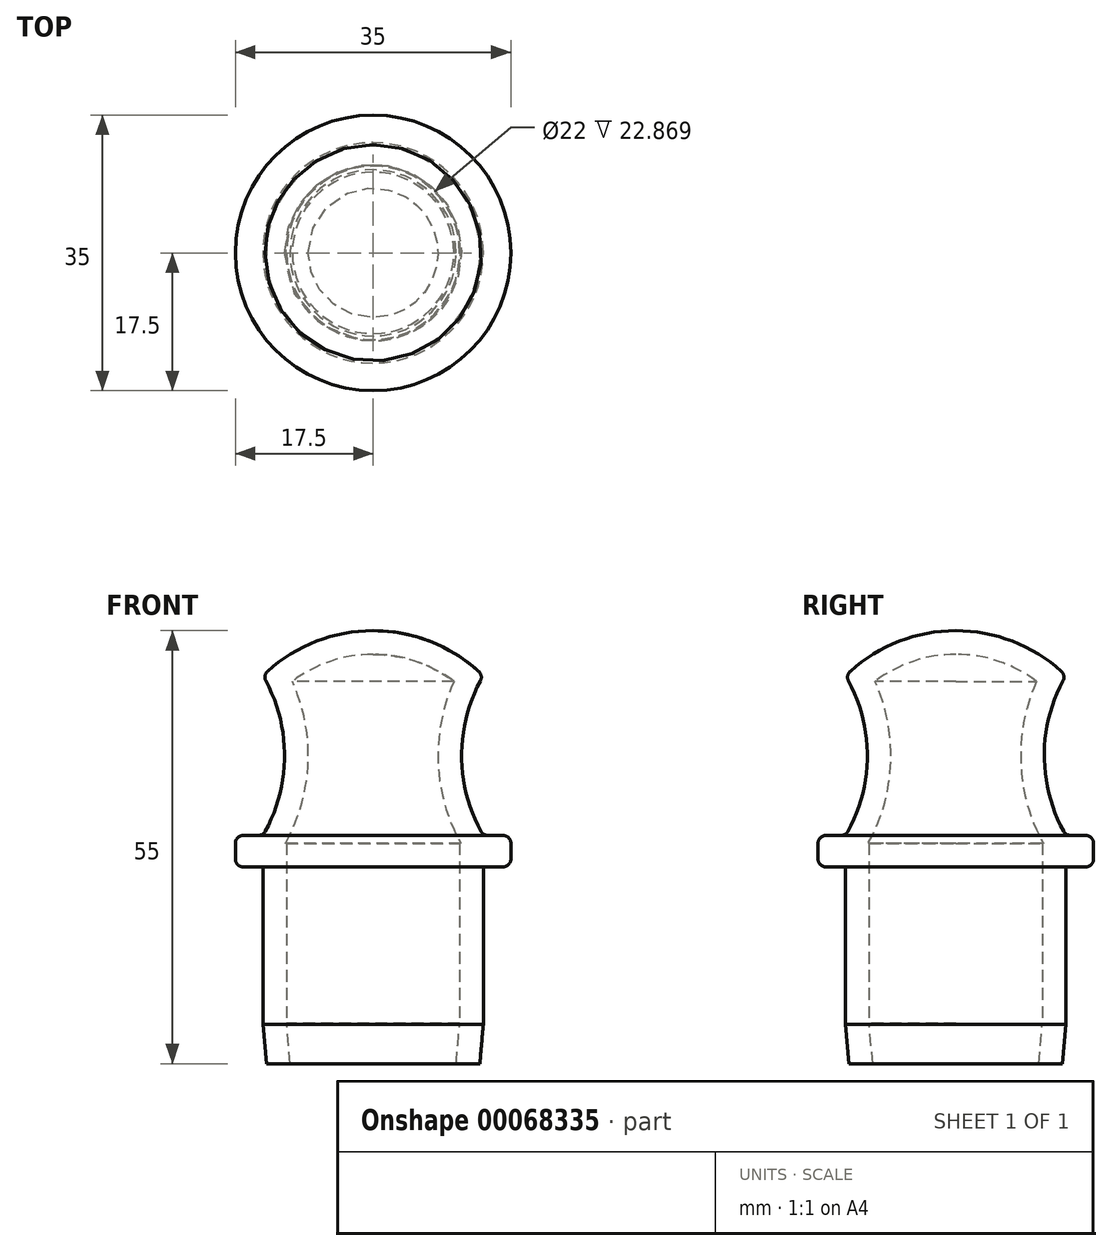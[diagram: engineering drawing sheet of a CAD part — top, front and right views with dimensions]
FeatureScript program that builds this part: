
annotation { "Feature Type Name" : "Feature", "Feature Type Description" : "" }
export const myFeature = defineFeature(function(context is Context, id is Id, definition is map)
    precondition{}
    {
        {
            var Q0;
            Q0=qCreatedBy(makeId("Top.planeOp"),FACE);
            var sketch = newSketch(context, id + "F0", { "sketchPlane" : qUnion([Q0])});
            skCircle(sketch, "E0", {"center": v(0, 0) * mm, "radius": 14 * mm});
            skSolve(sketch);
        }
        {
            var Q0;
            Q0 = qSketchRegion(id + "F0", true);
            extrude(context, id + "F1", {"entities" : qUnion([Q0]), "depth" : 25 * mm});
        }
        {
            var Q0;
            Q0=qCreatedBy(makeId("Front.planeOp"),FACE);
            var sketch = newSketch(context, id + "F2", { "sketchPlane" : qUnion([Q0])});
            skLineSegment(sketch, "E1.0.0", {"start": v(0, 25) * mm, "end": v(14, 25) * mm});
            skLineSegment(sketch, "E2", {"start": v(14, 25) * mm, "end": v(17.5, 25) * mm});
            skLineSegment(sketch, "E3", {"start": v(17.5, 25) * mm, "end": v(17.5, 29) * mm});
            skLineSegment(sketch, "E4", {"start": v(17.5, 29) * mm, "end": v(14, 29) * mm});
            skLineSegment(sketch, "E5", {"start": v(0, -0.93) * mm, "end": v(0, 40) * mm, "construction": true});
            skLineSegment(sketch, "E6", {"start": v(0, 55) * mm, "end": v(0, 25) * mm});
            skPoint(sketch, "E7.orphan", {"position": v(-14, 25) * mm});
            skArc(sketch, "E8", {"start": v(14, 49.28) * mm, "mid": v(11.24, 39.14) * mm, "end": v(14, 29) * mm});
            skArc(sketch, "E9", {"start": v(14, 49.28) * mm, "mid": v(7.56, 53.52) * mm, "end": v(0, 55) * mm});
            skSolve(sketch);
        }
        {
            var Q0;
            Q0 = qSketchRegion(id + "F2", true);
            var Q1;
            Q1=sQuery(id+"F2.wireOp",EDGE,"E5");
            revolve(context, id + "F3", {"operationType" : NewBodyOperationType.ADD, "entities" : qUnion([Q0]), "axis" : qUnion([Q1]), "revolveType" : RevolveType.FULL});
        }
        {
            var Q0;
            Q0=makeQuery(id+"F3.opRevolve","SWEPT_FACE",FACE,{"disambiguationData":[OSD([sQuery(id+"F2.wireOp",EDGE,"E8")])]});
            var Q1;
            Q1=makeQuery(id+"F3.opRevolve","SWEPT_FACE",FACE,{"disambiguationData":[OSD([sQuery(id+"F2.wireOp",EDGE,"E3")])]});
            fillet(context, id + "F4", {"entities" : qUnion([Q0, Q1]), "radius" : 1 * mm, "tangentPropagation" : true, "allowEdgeOverflow" : false});
        }
        {
            var Q0;
            Q0=makeQuery(id+"F1.opExtrude","CAP_EDGE",EDGE,{"disambiguationData":[OSD([sQuery(id+"F0.wireOp",EDGE,"E0")])],"isStart":true});
            chamfer(context, id + "F5", {"entities" : qUnion([Q0]), "chamferType" : ChamferType.OFFSET_ANGLE, "width" : 5 * mm, "oppositeDirection" : false, "angle" : 5 * degree, "tangentPropagation" : true});
        }
        {
            var Q0;
            Q0=makeQuery(id+"F1.opExtrude","CAP_FACE",FACE,{"disambiguationData":[OSD([sQuery(id+"F0.wireOp",EDGE,"E0")])],"isStart":true});
            shell(context, id + "F6", {"entities" : qUnion([Q0]), "thickness" : 3 * mm});
        }
    });
